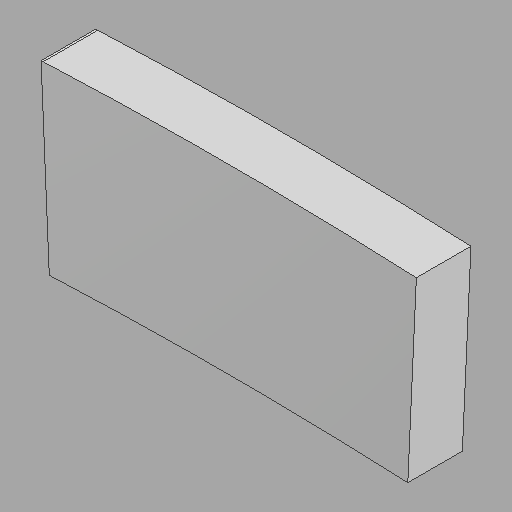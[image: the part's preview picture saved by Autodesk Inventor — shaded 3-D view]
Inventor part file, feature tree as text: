
AUTODESK INVENTOR PART (.ipt)
format: ipt  version: 2022.1 (Build 261234020, 234B)  size: 90,624 bytes
history: imported  units: in
note: dims shown in document units (in); Inventor stores cm internally (conversion verified against a paired STEP export)
features: imported_body x1
ambient origin geometry x8: Origin, YZ Plane, XZ Plane, XY Plane, X Axis, Y Axis, Z Axis, Center Point
bodies: Solid1 (imported_parasolid)
feature tree (1):
  imported_body  NMx_Import_Brep_tag  [imported B-rep: ~7 faces, bbox_mm=[1047.756234, 508.678939, 152.4]]
